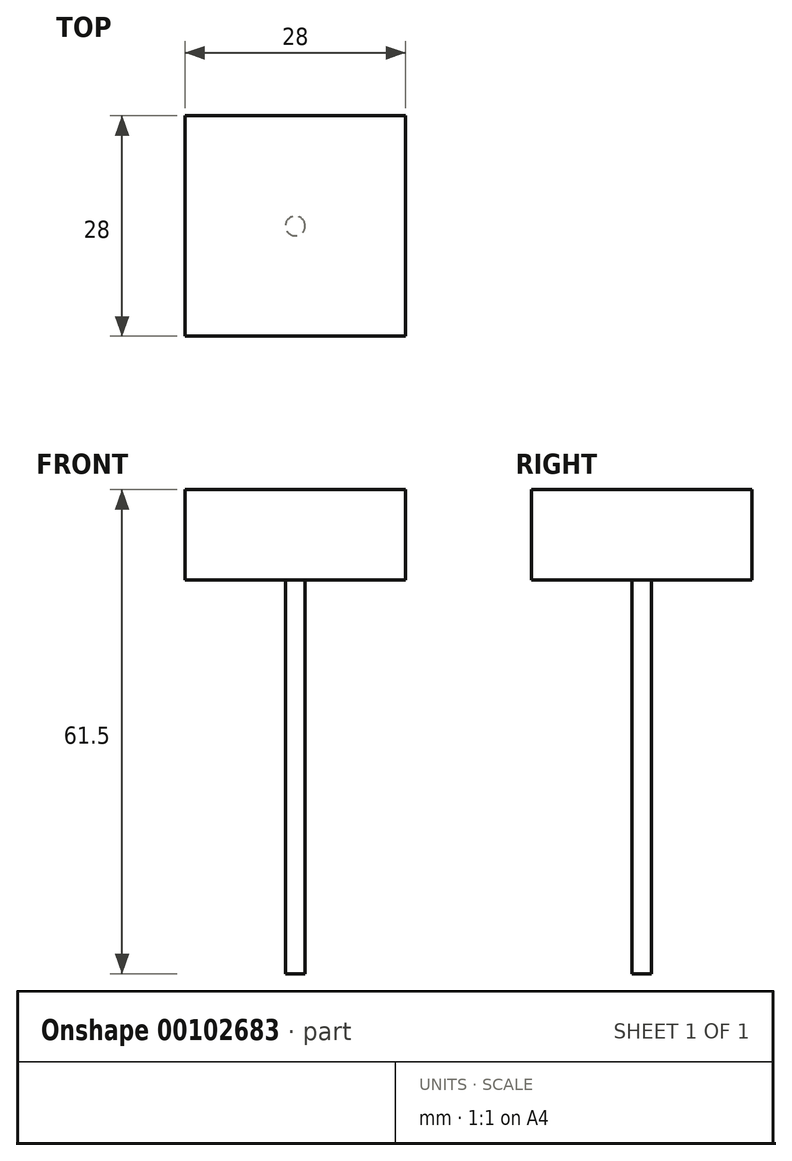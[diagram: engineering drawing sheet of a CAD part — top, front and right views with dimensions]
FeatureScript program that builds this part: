
annotation { "Feature Type Name" : "Feature", "Feature Type Description" : "" }
export const myFeature = defineFeature(function(context is Context, id is Id, definition is map)
    precondition{}
    {
        {
            var Q0;
            Q0=qCreatedBy(makeId("Top.planeOp"),FACE);
            var sketch = newSketch(context, id + "F0", { "sketchPlane" : qUnion([Q0])});
            skLineSegment(sketch, "E0.bottom", {"start": v(14, 14) * mm, "end": v(-14, 14) * mm});
            skLineSegment(sketch, "E0.top", {"start": v(14, -14) * mm, "end": v(-14, -14) * mm});
            skLineSegment(sketch, "E0.left", {"start": v(14, 14) * mm, "end": v(14, -14) * mm});
            skLineSegment(sketch, "E0.right", {"start": v(-14, 14) * mm, "end": v(-14, -14) * mm});
            skPoint(sketch, "E0.middle", {"position": v(0, 0) * mm});
            skSolve(sketch);
        }
        {
            var Q0;
            Q0=makeQuery(id+"F0.imprint","IMPRINT",FACE,{"disambiguationData":[TD([[makeQuery(id+"F0.imprint","IMPRINT",EDGE,{"derivedFrom":sQuery(id+"F0.wireOp",EDGE,"E0.bottom")}),1.0]])]});
            extrude(context, id + "F1", {"entities" : qUnion([Q0]), "depth" : 11.5 * mm});
        }
        {
            var Q0;
            Q0=makeQuery(id+"F1.opExtrude","CAP_FACE",FACE,{"disambiguationData":[OSD([sQuery(id+"F0.wireOp",EDGE,"E0.bottom"),sQuery(id+"F0.wireOp",EDGE,"E0.top"),sQuery(id+"F0.wireOp",EDGE,"E0.left"),sQuery(id+"F0.wireOp",EDGE,"E0.right")])],"isStart":true});
            var sketch = newSketch(context, id + "F2", { "sketchPlane" : qUnion([Q0])});
            skCircle(sketch, "E1", {"center": v(0, 0) * mm, "radius": 1.25 * mm});
            skSolve(sketch);
        }
        {
            var Q0;
            Q0=makeQuery(id+"F2.imprint","IMPRINT",FACE,{"disambiguationData":[TD([[makeQuery(id+"F2.imprint","IMPRINT",EDGE,{"derivedFrom":sQuery(id+"F2.wireOp",EDGE,"E1")}),1.0]])]});
            extrude(context, id + "F3", {"entities" : qUnion([Q0]), "operationType" : NewBodyOperationType.ADD, "depth" : 50 * mm});
        }
    });
